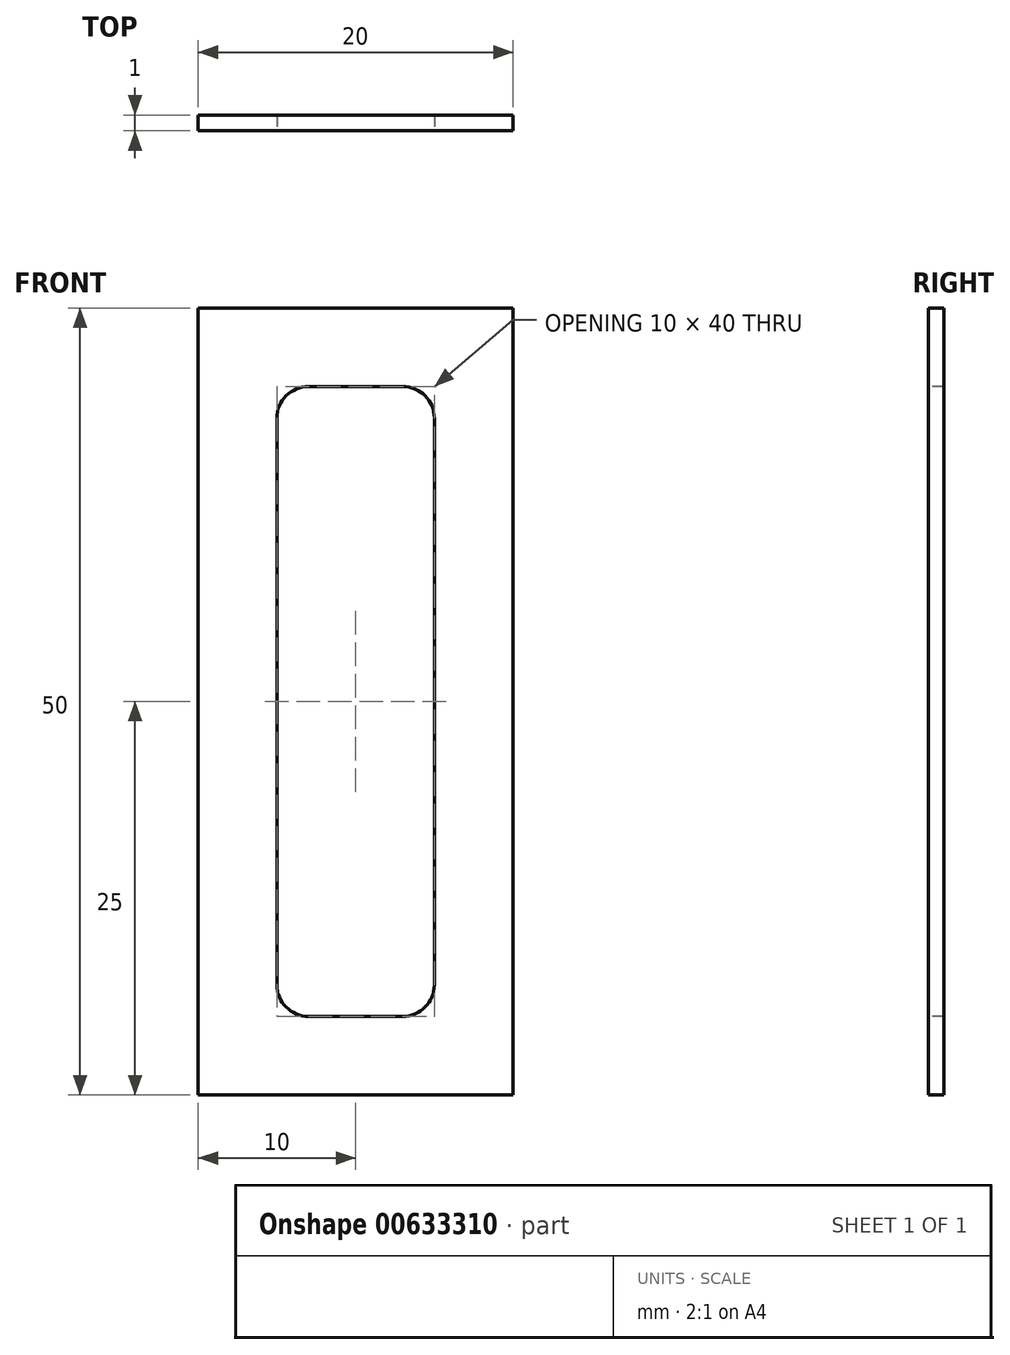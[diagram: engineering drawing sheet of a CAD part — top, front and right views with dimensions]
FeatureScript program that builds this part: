
annotation { "Feature Type Name" : "Feature", "Feature Type Description" : "" }
export const myFeature = defineFeature(function(context is Context, id is Id, definition is map)
    precondition{}
    {
        {
            var Q0;
            Q0=qCreatedBy(makeId("Front.planeOp"),FACE);
            var sketch = newSketch(context, id + "F0", { "sketchPlane" : qUnion([Q0])});
            skLineSegment(sketch, "E0.bottom", {"start": v(0, 0) * mm, "end": v(20, 0) * mm});
            skLineSegment(sketch, "E0.top", {"start": v(0, 50) * mm, "end": v(20, 50) * mm});
            skLineSegment(sketch, "E0.left", {"start": v(0, 0) * mm, "end": v(0, 50) * mm});
            skLineSegment(sketch, "E0.right", {"start": v(20, 0) * mm, "end": v(20, 50) * mm});
            skSolve(sketch);
        }
        {
            var Q0;
            Q0 = qSketchRegion(id + "F0", true);
            extrude(context, id + "F1", {"entities" : qUnion([Q0]), "depth" : 1 * mm, "offsetDistance" : 25 * mm});
        }
        {
            var Q0;
            Q0=makeQuery(id+"F1.opExtrude","CAP_FACE",FACE,{"disambiguationData":[OSD([sQuery(id+"F0.wireOp",EDGE,"E0.bottom"),sQuery(id+"F0.wireOp",EDGE,"E0.top"),sQuery(id+"F0.wireOp",EDGE,"E0.left"),sQuery(id+"F0.wireOp",EDGE,"E0.right")])],"isStart":false});
            var sketch = newSketch(context, id + "F2", { "sketchPlane" : qUnion([Q0])});
            skLineSegment(sketch, "E1.bottom", {"start": v(7, 5) * mm, "end": v(13, 5) * mm});
            skLineSegment(sketch, "E1.top", {"start": v(7, 45) * mm, "end": v(13, 45) * mm});
            skLineSegment(sketch, "E1.left", {"start": v(5, 7) * mm, "end": v(5, 43) * mm});
            skLineSegment(sketch, "E1.right", {"start": v(15, 7) * mm, "end": v(15, 43) * mm});
            skPoint(sketch, "E2.visualSharp", {"position": v(5, 45) * mm});
            skArc(sketch, "E2.filletArc", {"start": v(7, 45) * mm, "mid": v(5.59, 44.41) * mm, "end": v(5, 43) * mm});
            skPoint(sketch, "E3.visualSharp", {"position": v(15, 45) * mm});
            skArc(sketch, "E3.filletArc", {"start": v(15, 43) * mm, "mid": v(14.41, 44.41) * mm, "end": v(13, 45) * mm});
            skPoint(sketch, "E4.visualSharp", {"position": v(15, 5) * mm});
            skArc(sketch, "E4.filletArc", {"start": v(13, 5) * mm, "mid": v(14.41, 5.59) * mm, "end": v(15, 7) * mm});
            skPoint(sketch, "E5.visualSharp", {"position": v(5, 5) * mm});
            skArc(sketch, "E5.filletArc", {"start": v(5, 7) * mm, "mid": v(5.59, 5.59) * mm, "end": v(7, 5) * mm});
            skSolve(sketch);
        }
        {
            var Q0;
            Q0 = qSketchRegion(id + "F2", true);
            extrude(context, id + "F3", {"entities" : qUnion([Q0]), "operationType" : NewBodyOperationType.REMOVE, "endBound" : BoundingType.THROUGH_ALL, "oppositeDirection" : true, "depth" : 25 * mm, "offsetDistance" : 25 * mm});
        }
    });
